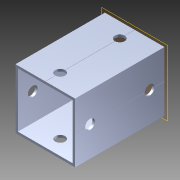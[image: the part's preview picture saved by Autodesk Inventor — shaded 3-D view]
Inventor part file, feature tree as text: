
AUTODESK INVENTOR PART (.ipt)
format: ipt  version: 2014 (Build 180170000, 170)  size: 1,186,304 bytes
history: native  units: in
note: dims shown in document units (in); Inventor stores cm internally (conversion verified against a paired STEP export)
features: extrude x2, sketch x2, pattern_circular x1, other x1, plane x1, imported_body x1
ambient origin geometry x8: Origin, YZ Plane, XZ Plane, XY Plane, X Axis, Y Axis, Z Axis, Center Point
bodies: Body1 (feature_tree)
feature tree (8):
  pattern_circular  "CirPattern2"
  other  "217-3426-STEP1"
  plane  "Work Plane1"
  extrude  "Extrusion1"  Depth=3937.0079in TaperAngle=0.0deg
  extrude  "Extrusion2"  [1 undecoded]
  imported_body  "Base1"
  sketch  "Sketch1"  dims[d0=-2.25in d1=3937.0079in d2=0.0in]
  sketch  "Sketch3"  dims[d3=0.25in d4=0.0in]
note: 1 required parameter value undecoded (feature->parameter linkage not recoverable at this tier; creation-order binding heuristic only, values carry confidence <= 0.55)
